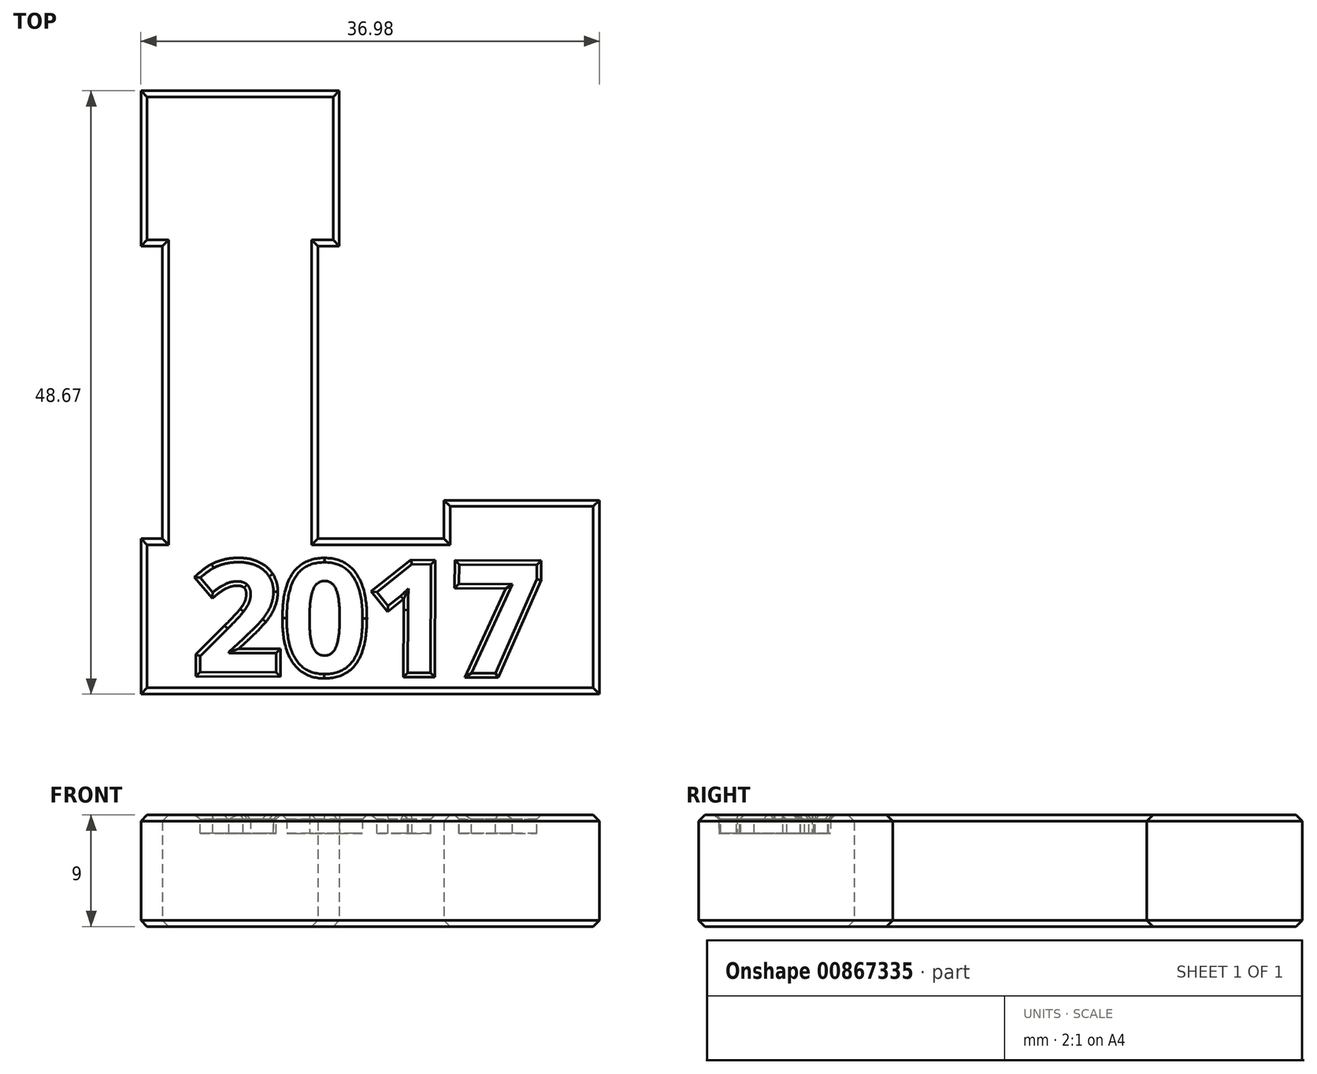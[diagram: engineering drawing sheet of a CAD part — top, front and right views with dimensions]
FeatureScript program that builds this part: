
annotation { "Feature Type Name" : "Feature", "Feature Type Description" : "" }
export const myFeature = defineFeature(function(context is Context, id is Id, definition is map)
    precondition{}
    {
        {
            var Q0;
            Q0=qCreatedBy(makeId("Top.planeOp"),FACE);
            var sketch = newSketch(context, id + "F0", { "sketchPlane" : qUnion([Q0])});
            skLineSegment(sketch, "E0", {"start": v(-7.5, 28) * mm, "end": v(8.5, 28) * mm});
            skLineSegment(sketch, "E1", {"start": v(8.5, 28) * mm, "end": v(8.5, 15.47) * mm});
            skLineSegment(sketch, "E2", {"start": v(8.5, 15.47) * mm, "end": v(6.77, 15.47) * mm});
            skLineSegment(sketch, "E3", {"start": v(6.77, 15.47) * mm, "end": v(6.77, -8.14) * mm});
            skLineSegment(sketch, "E4", {"start": v(6.77, -8.14) * mm, "end": v(16.95, -8.14) * mm});
            skLineSegment(sketch, "E5", {"start": v(16.95, -8.14) * mm, "end": v(16.95, -5.04) * mm});
            skLineSegment(sketch, "E6", {"start": v(16.95, -5.04) * mm, "end": v(29.48, -5.04) * mm});
            skLineSegment(sketch, "E7", {"start": v(29.48, -5.04) * mm, "end": v(29.48, -20.67) * mm});
            skLineSegment(sketch, "E8", {"start": v(-5.77, 15.47) * mm, "end": v(-7.5, 15.47) * mm});
            skLineSegment(sketch, "E9", {"start": v(-7.5, 15.47) * mm, "end": v(-7.5, 28) * mm});
            skLineSegment(sketch, "E10", {"start": v(29.48, -20.67) * mm, "end": v(-7.5, -20.67) * mm});
            skLineSegment(sketch, "E11", {"start": v(-7.5, -8.14) * mm, "end": v(-7.5, -20.67) * mm});
            skLineSegment(sketch, "E12", {"start": v(-7.5, -8.14) * mm, "end": v(-5.77, -8.14) * mm});
            skLineSegment(sketch, "E13", {"start": v(-5.77, -8.14) * mm, "end": v(-5.77, 15.47) * mm});
            skLineSegment(sketch, "E14", {"start": v(-5.77, 15.47) * mm, "end": v(6.77, 15.47) * mm, "construction": true});
            skLineSegment(sketch, "E15", {"start": v(6.77, -8.14) * mm, "end": v(6.77, -20.67) * mm, "construction": true});
            skSolve(sketch);
        }
        {
            var Q0;
            Q0=makeQuery(id+"F0.imprint","IMPRINT",FACE,{"disambiguationData":[TD([[makeQuery(id+"F0.imprint","IMPRINT",EDGE,{"derivedFrom":sQuery(id+"F0.wireOp",EDGE,"E0")}),-1.0]])]});
            extrude(context, id + "F1", {"entities" : qUnion([Q0]), "depth" : 9 * mm, "offsetDistance" : 25 * mm});
        }
        {
            var Q0;
            Q0=makeQuery(id+"F1.opExtrude","CAP_FACE",FACE,{"disambiguationData":[OSD([sQuery(id+"F0.wireOp",EDGE,"E0"),sQuery(id+"F0.wireOp",EDGE,"E1"),sQuery(id+"F0.wireOp",EDGE,"E2"),sQuery(id+"F0.wireOp",EDGE,"E3"),sQuery(id+"F0.wireOp",EDGE,"E4"),sQuery(id+"F0.wireOp",EDGE,"E5"),sQuery(id+"F0.wireOp",EDGE,"E6"),sQuery(id+"F0.wireOp",EDGE,"E7"),sQuery(id+"F0.wireOp",EDGE,"E8"),sQuery(id+"F0.wireOp",EDGE,"E9"),sQuery(id+"F0.wireOp",EDGE,"E10"),sQuery(id+"F0.wireOp",EDGE,"E11"),sQuery(id+"F0.wireOp",EDGE,"E12"),sQuery(id+"F0.wireOp",EDGE,"E13")])],"isStart":false});
            var sketch = newSketch(context, id + "F2", { "sketchPlane" : qUnion([Q0])});
            skText(sketch, "E16", { "text": "2017", "fontName": "OpenSans-Bold.ttf"});
            skPoint(sketch, "E17", {"position": v(11, -20.67) * mm});
            const initialGuessF2  = {"E16": [-0.0032, -0.0189, 1, -0.00327, 0.00883]};
            skSetInitialGuess(sketch, initialGuessF2);
            skSolve(sketch);
        }
        {
            var Q0;
            Q0 = qSketchRegion(id + "F2", true);
            extrude(context, id + "F3", {"entities" : qUnion([Q0]), "operationType" : NewBodyOperationType.REMOVE, "oppositeDirection" : true, "depth" : 1.5 * mm, "offsetDistance" : 25 * mm});
        }
        {
            var Q0;
            Q0=makeQuery(id+"F3.boolean.opBoolean","COPY",EDGE,{"derivedFrom":makeQuery(id+"F3.opExtrude","CAP_EDGE",EDGE,{"disambiguationData":[OSD([sQuery(id+"F2.wireOp",EDGE,"E16.sketch_text.stroke-11")])],"isStart":true})});
            var Q1;
            Q1=makeQuery(id+"F3.boolean.opBoolean","COPY",EDGE,{"derivedFrom":makeQuery(id+"F3.opExtrude","CAP_EDGE",EDGE,{"disambiguationData":[OSD([sQuery(id+"F2.wireOp",EDGE,"E16.sketch_text.stroke-10")])],"isStart":true})});
            var Q2;
            Q2=makeQuery(id+"F3.boolean.opBoolean","COPY",EDGE,{"derivedFrom":makeQuery(id+"F3.opExtrude","CAP_EDGE",EDGE,{"disambiguationData":[OSD([sQuery(id+"F2.wireOp",EDGE,"E16.sketch_text.stroke-7")])],"isStart":true})});
            var Q3;
            Q3=makeQuery(id+"F3.boolean.opBoolean","COPY",EDGE,{"derivedFrom":makeQuery(id+"F3.opExtrude","CAP_EDGE",EDGE,{"disambiguationData":[OSD([sQuery(id+"F2.wireOp",EDGE,"E16.sketch_text.stroke-2")])],"isStart":true})});
            var Q4;
            Q4=makeQuery(id+"F3.boolean.opBoolean","COPY",EDGE,{"derivedFrom":makeQuery(id+"F3.opExtrude","CAP_EDGE",EDGE,{"disambiguationData":[OSD([sQuery(id+"F2.wireOp",EDGE,"E16.sketch_text.stroke-1")])],"isStart":true})});
            var Q5;
            Q5=makeQuery(id+"F3.boolean.opBoolean","COPY",EDGE,{"derivedFrom":makeQuery(id+"F3.opExtrude","CAP_EDGE",EDGE,{"disambiguationData":[OSD([sQuery(id+"F2.wireOp",EDGE,"E16.sketch_text.stroke-0")])],"isStart":true})});
            var Q6;
            Q6=makeQuery(id+"F3.boolean.opBoolean","COPY",EDGE,{"derivedFrom":makeQuery(id+"F3.opExtrude","CAP_EDGE",EDGE,{"disambiguationData":[OSD([sQuery(id+"F2.wireOp",EDGE,"E16.sketch_text.stroke-23")])],"isStart":true})});
            var Q7;
            Q7=makeQuery(id+"F3.boolean.opBoolean","COPY",EDGE,{"derivedFrom":makeQuery(id+"F3.opExtrude","CAP_EDGE",EDGE,{"disambiguationData":[OSD([sQuery(id+"F2.wireOp",EDGE,"E16.sketch_text.stroke-22")])],"isStart":true})});
            var Q8;
            Q8=makeQuery(id+"F3.boolean.opBoolean","COPY",EDGE,{"derivedFrom":makeQuery(id+"F3.opExtrude","CAP_EDGE",EDGE,{"disambiguationData":[OSD([sQuery(id+"F2.wireOp",EDGE,"E16.sketch_text.stroke-28")])],"isStart":true})});
            var Q9;
            Q9=makeQuery(id+"F3.boolean.opBoolean","COPY",EDGE,{"derivedFrom":makeQuery(id+"F3.opExtrude","CAP_EDGE",EDGE,{"disambiguationData":[OSD([sQuery(id+"F2.wireOp",EDGE,"E16.sketch_text.stroke-39")])],"isStart":true})});
            var Q10;
            Q10=makeQuery(id+"F3.boolean.opBoolean","COPY",EDGE,{"derivedFrom":makeQuery(id+"F3.opExtrude","CAP_EDGE",EDGE,{"disambiguationData":[OSD([sQuery(id+"F2.wireOp",EDGE,"E16.sketch_text.stroke-47")])],"isStart":true})});
            var Q11;
            Q11=makeQuery(id+"F3.boolean.opBoolean","COPY",EDGE,{"derivedFrom":makeQuery(id+"F3.opExtrude","CAP_EDGE",EDGE,{"disambiguationData":[OSD([sQuery(id+"F2.wireOp",EDGE,"E16.sketch_text.stroke-48")])],"isStart":true})});
            var Q12;
            Q12=makeQuery(id+"F3.boolean.opBoolean","COPY",EDGE,{"derivedFrom":makeQuery(id+"F3.opExtrude","CAP_EDGE",EDGE,{"disambiguationData":[OSD([sQuery(id+"F2.wireOp",EDGE,"E16.sketch_text.stroke-46")])],"isStart":true})});
            var Q13;
            Q13=makeQuery(id+"F3.boolean.opBoolean","COPY",EDGE,{"derivedFrom":makeQuery(id+"F3.opExtrude","CAP_EDGE",EDGE,{"disambiguationData":[OSD([sQuery(id+"F2.wireOp",EDGE,"E16.sketch_text.stroke-45")])],"isStart":true})});
            var Q14;
            Q14=makeQuery(id+"F3.boolean.opBoolean","COPY",EDGE,{"derivedFrom":makeQuery(id+"F3.opExtrude","CAP_EDGE",EDGE,{"disambiguationData":[OSD([sQuery(id+"F2.wireOp",EDGE,"E16.sketch_text.stroke-42")])],"isStart":true})});
            var Q15;
            Q15=makeQuery(id+"F3.boolean.opBoolean","COPY",EDGE,{"derivedFrom":makeQuery(id+"F3.opExtrude","CAP_EDGE",EDGE,{"disambiguationData":[OSD([sQuery(id+"F2.wireOp",EDGE,"E16.sketch_text.stroke-49")])],"isStart":true})});
            var Q16;
            Q16=makeQuery(id+"F3.boolean.opBoolean","COPY",EDGE,{"derivedFrom":makeQuery(id+"F3.opExtrude","CAP_EDGE",EDGE,{"disambiguationData":[OSD([sQuery(id+"F2.wireOp",EDGE,"E16.sketch_text.stroke-40")])],"isStart":true})});
            var Q17;
            Q17=makeQuery(id+"F3.boolean.opBoolean","COPY",EDGE,{"derivedFrom":makeQuery(id+"F3.opExtrude","CAP_EDGE",EDGE,{"disambiguationData":[OSD([sQuery(id+"F2.wireOp",EDGE,"E16.sketch_text.stroke-51")])],"isStart":true})});
            var Q18;
            Q18=makeQuery(id+"F3.boolean.opBoolean","COPY",EDGE,{"derivedFrom":makeQuery(id+"F3.opExtrude","CAP_EDGE",EDGE,{"disambiguationData":[OSD([sQuery(id+"F2.wireOp",EDGE,"E16.sketch_text.stroke-52")])],"isStart":true})});
            var Q19;
            Q19=makeQuery(id+"F3.boolean.opBoolean","COPY",EDGE,{"derivedFrom":makeQuery(id+"F3.opExtrude","CAP_EDGE",EDGE,{"disambiguationData":[OSD([sQuery(id+"F2.wireOp",EDGE,"E16.sketch_text.stroke-53")])],"isStart":true})});
            var Q20;
            Q20=makeQuery(id+"F3.boolean.opBoolean","COPY",EDGE,{"derivedFrom":makeQuery(id+"F3.opExtrude","CAP_EDGE",EDGE,{"disambiguationData":[OSD([sQuery(id+"F2.wireOp",EDGE,"E16.sketch_text.stroke-54")])],"isStart":true})});
            var Q21;
            Q21=makeQuery(id+"F3.boolean.opBoolean","COPY",EDGE,{"derivedFrom":makeQuery(id+"F3.opExtrude","CAP_EDGE",EDGE,{"disambiguationData":[OSD([sQuery(id+"F2.wireOp",EDGE,"E16.sketch_text.stroke-55")])],"isStart":true})});
            var Q22;
            Q22=makeQuery(id+"F3.boolean.opBoolean","COPY",EDGE,{"derivedFrom":makeQuery(id+"F3.opExtrude","CAP_EDGE",EDGE,{"disambiguationData":[OSD([sQuery(id+"F2.wireOp",EDGE,"E16.sketch_text.stroke-56")])],"isStart":true})});
            var Q23;
            Q23=makeQuery(id+"F3.boolean.opBoolean","COPY",EDGE,{"derivedFrom":makeQuery(id+"F3.opExtrude","CAP_EDGE",EDGE,{"disambiguationData":[OSD([sQuery(id+"F2.wireOp",EDGE,"E16.sketch_text.stroke-50")])],"isStart":true})});
            chamfer(context, id + "F4", {"entities" : qUnion([Q0, Q1, Q2, Q3, Q4, Q5, Q6, Q7, Q8, Q9, Q10, Q11, Q12, Q13, Q14, Q15, Q16, Q17, Q18, Q19, Q20, Q21, Q22, Q23]), "width" : .35 * mm, "tangentPropagation" : true});
        }
        {
            var Q0;
            Q0=makeQuery(id+"F1.opExtrude","CAP_EDGE",EDGE,{"disambiguationData":[OSD([sQuery(id+"F0.wireOp",EDGE,"E7")])],"isStart":false});
            var Q1;
            Q1=makeQuery(id+"F1.opExtrude","CAP_EDGE",EDGE,{"disambiguationData":[OSD([sQuery(id+"F0.wireOp",EDGE,"E6")])],"isStart":false});
            var Q2;
            Q2=makeQuery(id+"F1.opExtrude","CAP_EDGE",EDGE,{"disambiguationData":[OSD([sQuery(id+"F0.wireOp",EDGE,"E5")])],"isStart":false});
            var Q3;
            Q3=makeQuery(id+"F1.opExtrude","CAP_EDGE",EDGE,{"disambiguationData":[OSD([sQuery(id+"F0.wireOp",EDGE,"E4")])],"isStart":false});
            var Q4;
            Q4=makeQuery(id+"F1.opExtrude","CAP_EDGE",EDGE,{"disambiguationData":[OSD([sQuery(id+"F0.wireOp",EDGE,"E3")])],"isStart":false});
            var Q5;
            Q5=makeQuery(id+"F1.opExtrude","CAP_EDGE",EDGE,{"disambiguationData":[OSD([sQuery(id+"F0.wireOp",EDGE,"E2")])],"isStart":false});
            var Q6;
            Q6=makeQuery(id+"F1.opExtrude","CAP_EDGE",EDGE,{"disambiguationData":[OSD([sQuery(id+"F0.wireOp",EDGE,"E1")])],"isStart":false});
            var Q7;
            Q7=makeQuery(id+"F1.opExtrude","CAP_EDGE",EDGE,{"disambiguationData":[OSD([sQuery(id+"F0.wireOp",EDGE,"E0")])],"isStart":false});
            var Q8;
            Q8=makeQuery(id+"F1.opExtrude","CAP_EDGE",EDGE,{"disambiguationData":[OSD([sQuery(id+"F0.wireOp",EDGE,"E9")])],"isStart":false});
            var Q9;
            Q9=makeQuery(id+"F1.opExtrude","CAP_EDGE",EDGE,{"disambiguationData":[OSD([sQuery(id+"F0.wireOp",EDGE,"E8")])],"isStart":false});
            var Q10;
            Q10=makeQuery(id+"F1.opExtrude","CAP_EDGE",EDGE,{"disambiguationData":[OSD([sQuery(id+"F0.wireOp",EDGE,"E13")])],"isStart":false});
            var Q11;
            Q11=makeQuery(id+"F1.opExtrude","CAP_EDGE",EDGE,{"disambiguationData":[OSD([sQuery(id+"F0.wireOp",EDGE,"E12")])],"isStart":false});
            var Q12;
            Q12=makeQuery(id+"F1.opExtrude","CAP_EDGE",EDGE,{"disambiguationData":[OSD([sQuery(id+"F0.wireOp",EDGE,"E11")])],"isStart":false});
            var Q13;
            Q13=makeQuery(id+"F1.opExtrude","CAP_EDGE",EDGE,{"disambiguationData":[OSD([sQuery(id+"F0.wireOp",EDGE,"E10")])],"isStart":false});
            var Q14;
            Q14=makeQuery(id+"F1.opExtrude","CAP_FACE",FACE,{"disambiguationData":[OSD([sQuery(id+"F0.wireOp",EDGE,"E0"),sQuery(id+"F0.wireOp",EDGE,"E1"),sQuery(id+"F0.wireOp",EDGE,"E2"),sQuery(id+"F0.wireOp",EDGE,"E3"),sQuery(id+"F0.wireOp",EDGE,"E4"),sQuery(id+"F0.wireOp",EDGE,"E5"),sQuery(id+"F0.wireOp",EDGE,"E6"),sQuery(id+"F0.wireOp",EDGE,"E7"),sQuery(id+"F0.wireOp",EDGE,"E8"),sQuery(id+"F0.wireOp",EDGE,"E9"),sQuery(id+"F0.wireOp",EDGE,"E10"),sQuery(id+"F0.wireOp",EDGE,"E11"),sQuery(id+"F0.wireOp",EDGE,"E12"),sQuery(id+"F0.wireOp",EDGE,"E13")])],"isStart":true});
            chamfer(context, id + "F5", {"entities" : qUnion([Q0, Q1, Q2, Q3, Q4, Q5, Q6, Q7, Q8, Q9, Q10, Q11, Q12, Q13, Q14]), "width" : .5 * mm, "tangentPropagation" : true});
        }
    });
